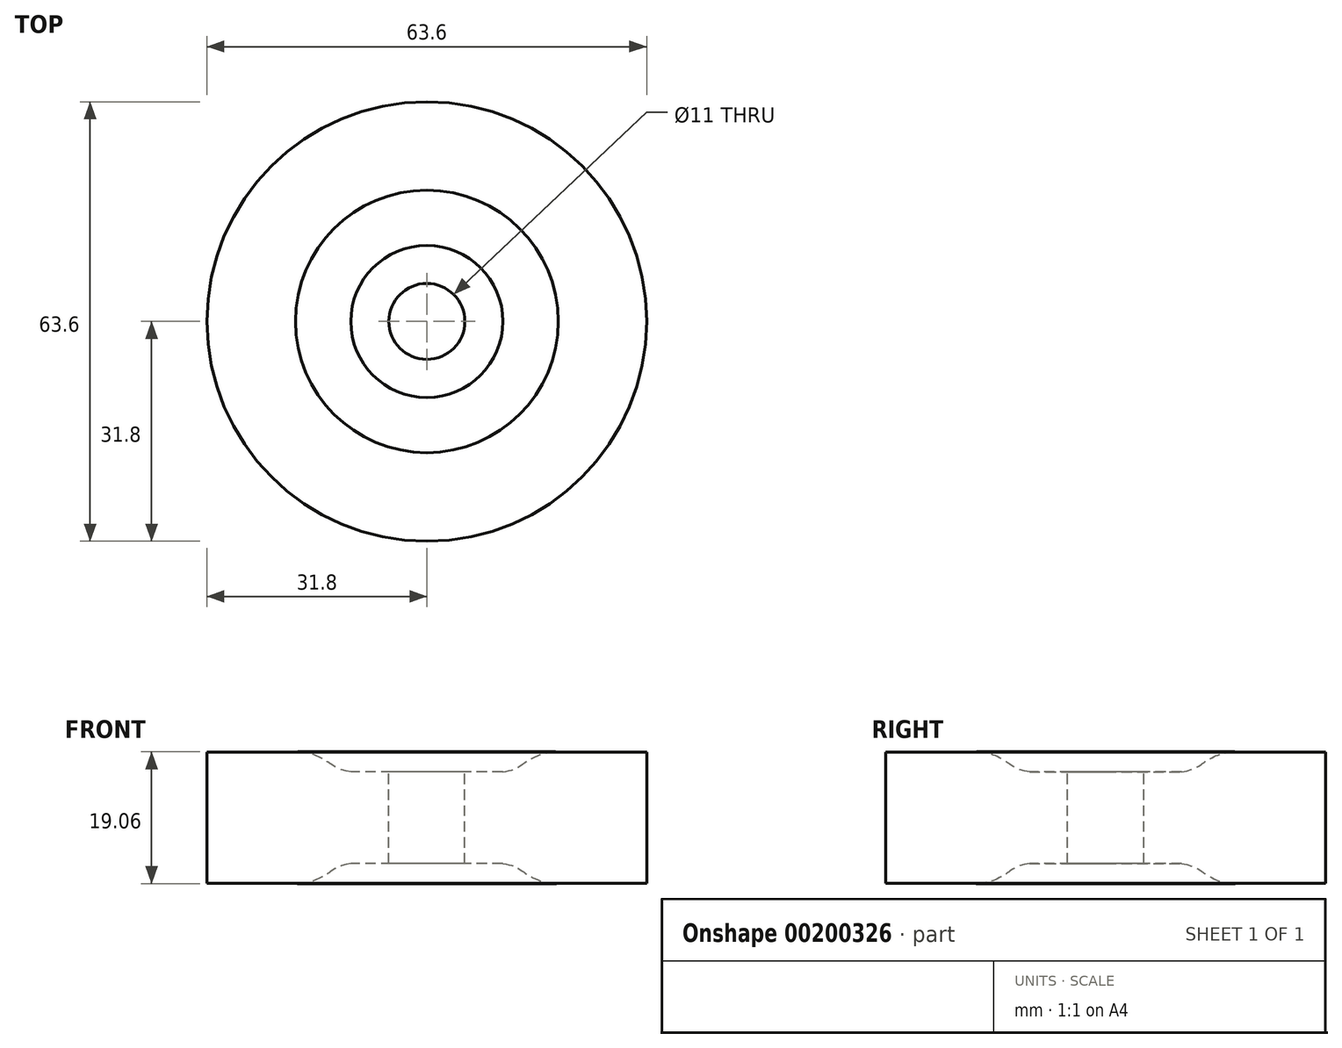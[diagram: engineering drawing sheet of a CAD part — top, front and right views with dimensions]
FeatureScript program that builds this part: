
annotation { "Feature Type Name" : "Feature", "Feature Type Description" : "" }
export const myFeature = defineFeature(function(context is Context, id is Id, definition is map)
    precondition{}
    {
        {
            var Q0;
            Q0=qCreatedBy(makeId("Front.planeOp"),FACE);
            var sketch = newSketch(context, id + "F0", { "sketchPlane" : qUnion([Q0])});
            skLineSegment(sketch, "E0", {"start": v(0, 13.04) * mm, "end": v(0, -14) * mm, "construction": true});
            skLineSegment(sketch, "E1", {"start": v(5.5, 6.62) * mm, "end": v(5.5, -6.62) * mm});
            skLineSegment(sketch, "E2", {"start": v(5.5, -6.62) * mm, "end": v(11, -6.62) * mm});
            skLineSegment(sketch, "E3", {"start": v(19, -9.5) * mm, "end": v(19, 9.5) * mm});
            skLineSegment(sketch, "E4", {"start": v(11, 6.62) * mm, "end": v(5.5, 6.62) * mm});
            skLineSegment(sketch, "E5", {"start": v(0, 0) * mm, "end": v(5.5, 0) * mm, "construction": true});
            skLineSegment(sketch, "E6", {"start": v(5.5, 0) * mm, "end": v(19, 0) * mm, "construction": true});
            skFitSpline(sketch, "E7", {"points": [v(11, 6.62) * mm, v(13.82, 7.72) * mm, v(14.27, 8.05) * mm, v(19, 9.5) * mm], "startDerivative": vector(12.01, 1.48) * mm, "endDerivative": vector(12.77, -1.53) * mm});
            skFitSpline(sketch, "E8", {"points": [v(11, -6.62) * mm, v(13.82, -7.72) * mm, v(14.27, -8.05) * mm, v(19, -9.5) * mm], "startDerivative": vector(12.01, -1.48) * mm, "endDerivative": vector(12.77, 1.53) * mm});
            skLineSegment(sketch, "E9", {"start": v(14.27, 8.05) * mm, "end": v(14.27, -8.05) * mm, "construction": true});
            skPoint(sketch, "E10", {"position": v(14.27, 0) * mm});
            skPoint(sketch, "E11", {"position": v(13.82, 0) * mm});
            skLineSegment(sketch, "E12", {"start": v(17, 9.74) * mm, "end": v(17, -9.74) * mm, "construction": true});
            skPoint(sketch, "E13", {"position": v(12.48, 0) * mm});
            skPoint(sketch, "E14", {"position": v(17, 0) * mm});
            skLineSegment(sketch, "E15", {"start": v(13.82, 7.72) * mm, "end": v(13.82, -7.72) * mm, "construction": true});
            skLineSegment(sketch, "E16", {"start": v(12.48, 6.8) * mm, "end": v(12.48, -6.8) * mm, "construction": true});
            skLineSegment(sketch, "E17", {"start": v(19, 9.5) * mm, "end": v(31.8, 9.5) * mm});
            skLineSegment(sketch, "E18", {"start": v(31.8, 9.5) * mm, "end": v(31.8, -9.5) * mm});
            skLineSegment(sketch, "E19", {"start": v(31.8, -9.5) * mm, "end": v(19, -9.5) * mm});
            skSolve(sketch);
        }
        {
            var Q0;
            Q0=qSketchRegion(id+"F0",true);
            var Q1;
            Q1=sQuery(id+"F0.wireOp",EDGE,"E0");
            revolve(context, id + "F1", {"entities" : qUnion([Q0]), "axis" : qUnion([Q1]), "revolveType" : RevolveType.FULL});
        }
    });
